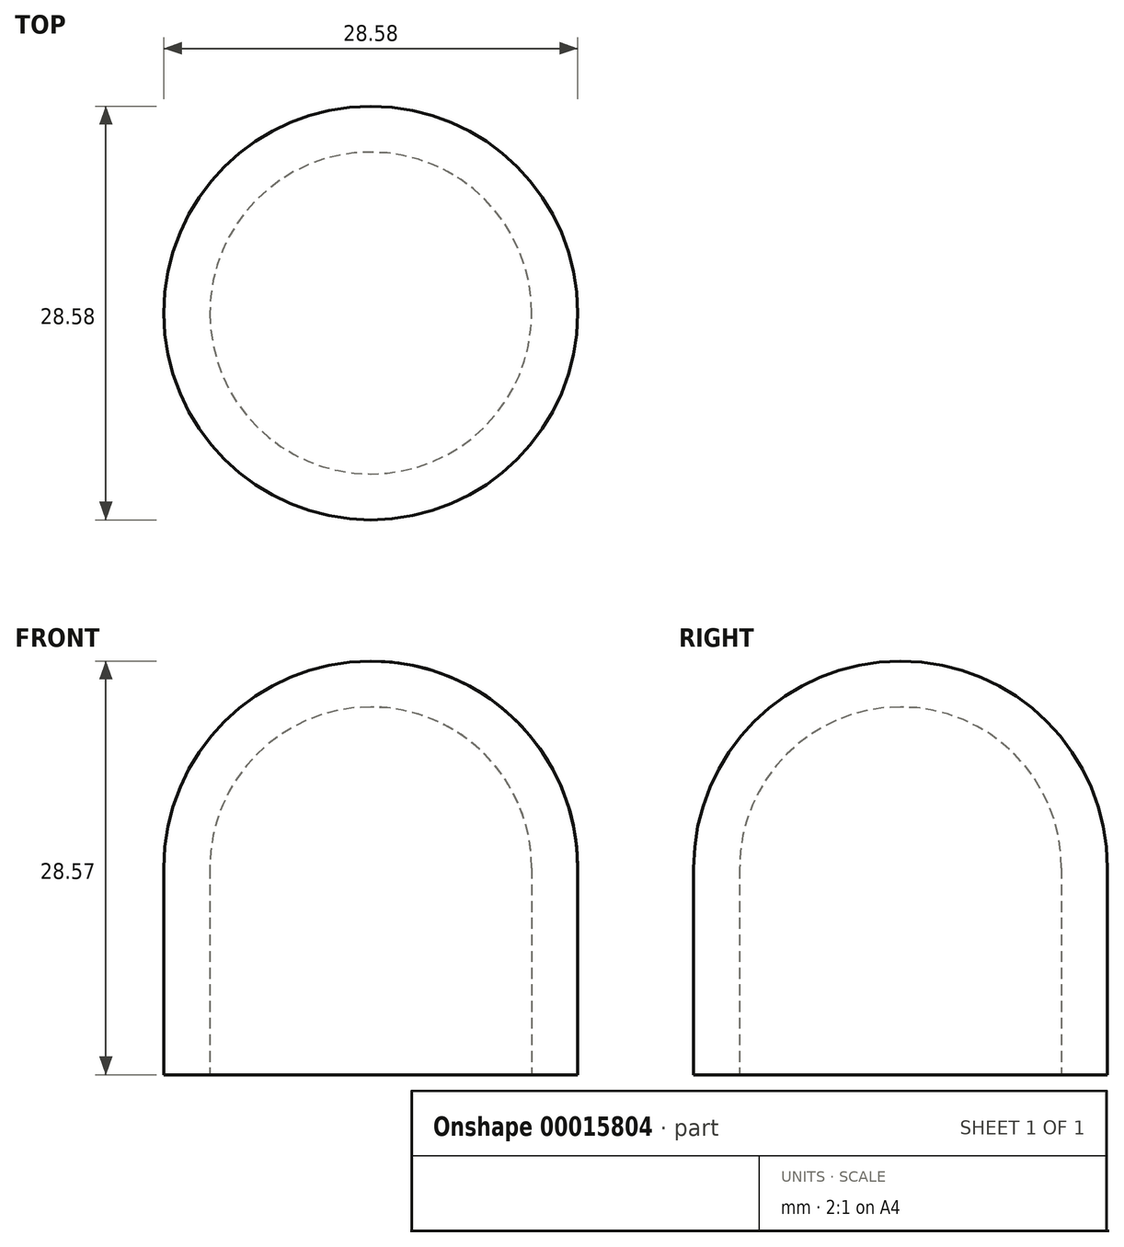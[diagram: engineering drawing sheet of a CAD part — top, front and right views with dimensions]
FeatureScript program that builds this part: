
annotation { "Feature Type Name" : "Feature", "Feature Type Description" : "" }
export const myFeature = defineFeature(function(context is Context, id is Id, definition is map)
    precondition{}
    {
        {
            var Q0;
            Q0=qCreatedBy(makeId("Top.planeOp"),FACE);
            var sketch = newSketch(context, id + "F0", { "sketchPlane" : qUnion([Q0])});
            skCircle(sketch, "E0", {"center": v(0, 0) * mm, "radius": 14.29 * mm});
            skSolve(sketch);
        }
        {
            var Q0;
            Q0=qSketchRegion(id+"F0",true);
            extrude(context, id + "F1", {"entities" : qUnion([Q0]), "depth" : 28.57 * mm});
        }
        {
            var Q0;
            Q0=makeQuery(id+"F1.opExtrude","CAP_EDGE",EDGE,{"disambiguationData":[OSD([sQuery(id+"F0.wireOp",EDGE,"E0")])],"isStart":false});
            fillet(context, id + "F2", {"entities" : qUnion([Q0]), "radius" : 14.29 * mm, "tangentPropagation" : true, "allowEdgeOverflow" : false});
        }
        {
            var Q0;
            Q0=makeQuery(id+"F1.opExtrude","CAP_FACE",FACE,{"disambiguationData":[OSD([sQuery(id+"F0.wireOp",EDGE,"E0")])],"isStart":true});
            shell(context, id + "F3", {"entities" : qUnion([Q0]), "thickness" : 3.17 * mm});
        }
    });
